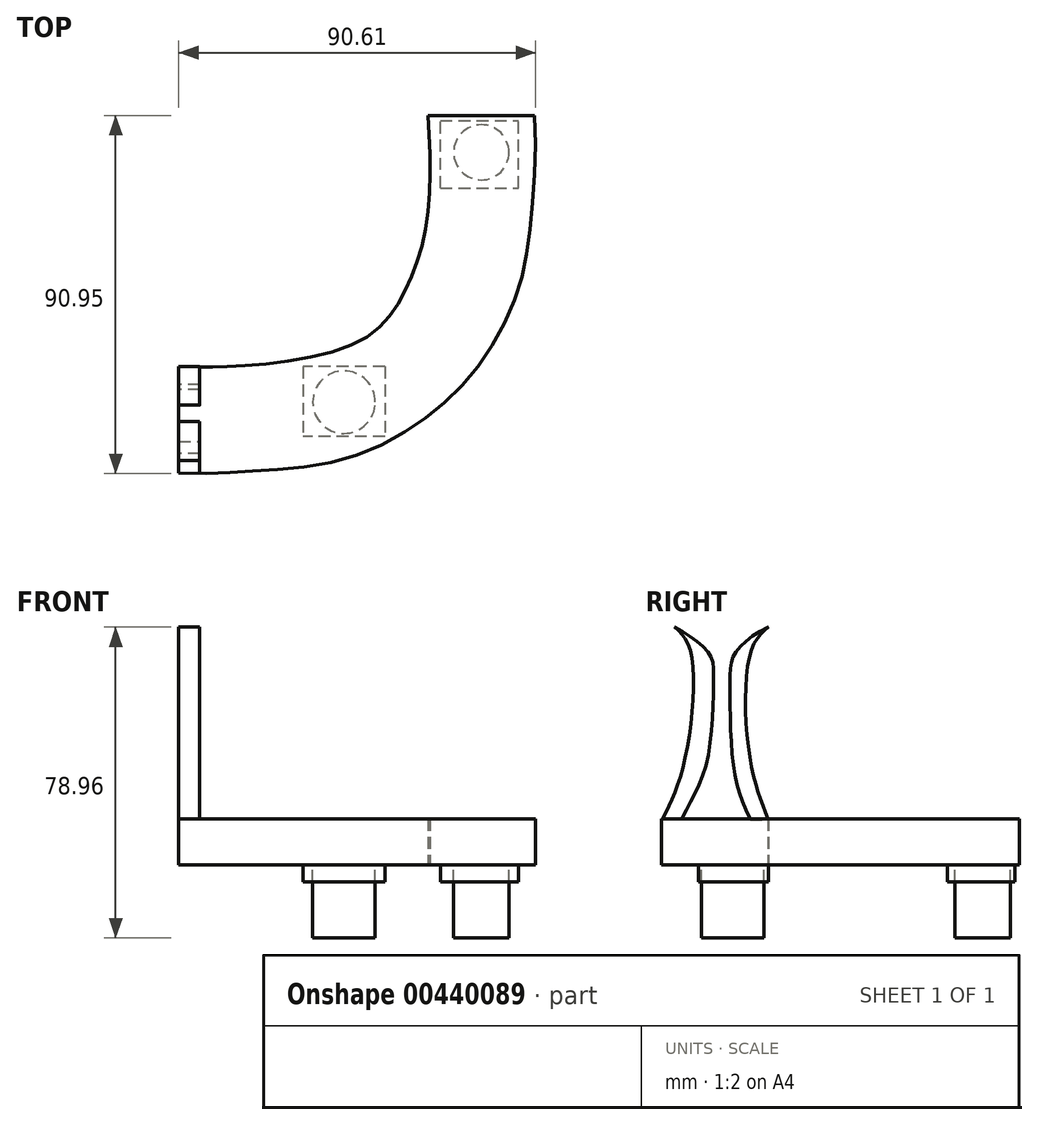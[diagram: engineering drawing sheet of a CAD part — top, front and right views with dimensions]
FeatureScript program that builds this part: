
annotation { "Feature Type Name" : "Feature", "Feature Type Description" : "" }
export const myFeature = defineFeature(function(context is Context, id is Id, definition is map)
    precondition{}
    {
        {
            var Q0;
            Q0=qCreatedBy(makeId("Top.planeOp"),FACE);
            var sketch = newSketch(context, id + "F0", { "sketchPlane" : qUnion([Q0])});
            skLineSegment(sketch, "E0.bottom", {"start": v(-66.47, 45.42) * mm, "end": v(-86.33, 45.42) * mm});
            skLineSegment(sketch, "E0.top", {"start": v(-66.47, 62.56) * mm, "end": v(-86.33, 62.56) * mm});
            skLineSegment(sketch, "E0.left", {"start": v(-66.47, 45.42) * mm, "end": v(-66.47, 62.56) * mm});
            skLineSegment(sketch, "E0.right", {"start": v(-86.33, 45.42) * mm, "end": v(-86.33, 62.56) * mm});
            skLineSegment(sketch, "E1.bottom", {"start": v(-52.34, 0) * mm, "end": v(-31.58, 0) * mm});
            skLineSegment(sketch, "E1.top", {"start": v(-52.34, -17.75) * mm, "end": v(-31.58, -17.75) * mm});
            skLineSegment(sketch, "E1.left", {"start": v(-52.34, 0) * mm, "end": v(-52.34, -17.75) * mm});
            skLineSegment(sketch, "E1.right", {"start": v(-31.58, 0) * mm, "end": v(-31.58, -17.75) * mm});
            skCircle(sketch, "E2", {"center": v(-76.4, 54) * mm, "radius": 7.19 * mm, "construction": true});
            skPoint(sketch, "E2.centerSnap0", {"position": v(-86.33, 54) * mm});
            skLineSegment(sketch, "E3.MirrorCS", {"start": v(66.47, 62.56) * mm, "end": v(86.33, 62.56) * mm});
            skLineSegment(sketch, "E4.MirrorCS", {"start": v(66.47, 45.42) * mm, "end": v(66.47, 62.56) * mm});
            skLineSegment(sketch, "E5.MirrorCS", {"start": v(66.47, 45.42) * mm, "end": v(86.33, 45.42) * mm});
            skLineSegment(sketch, "E6.MirrorCS", {"start": v(86.33, 45.42) * mm, "end": v(86.33, 62.56) * mm});
            skCircle(sketch, "E7.MirrorC", {"center": v(76.4, 54) * mm, "radius": 7.19 * mm, "construction": true});
            skLineSegment(sketch, "E8.MirrorCS", {"start": v(52.34, 0) * mm, "end": v(31.58, 0) * mm});
            skLineSegment(sketch, "E9.MirrorCS", {"start": v(31.58, 0) * mm, "end": v(31.58, -17.75) * mm});
            skLineSegment(sketch, "E10.MirrorCS", {"start": v(52.34, -17.75) * mm, "end": v(31.58, -17.75) * mm});
            skLineSegment(sketch, "E11.MirrorCS", {"start": v(52.34, 0) * mm, "end": v(52.34, -17.75) * mm});
            skSolve(sketch);
        }
        {
            var Q0;
            Q0=qCreatedBy(makeId("Top.planeOp"),FACE);
            var sketch = newSketch(context, id + "F1", { "sketchPlane" : qUnion([Q0])});
            skCircle(sketch, "E12.MirrorC", {"center": v(76.85, 54.44) * mm, "radius": 7.02 * mm});
            skSolve(sketch);
        }
        {
            var Q0;
            Q0=qSketchRegion(id+"F1",true);
            extrude(context, id + "F2", {"entities" : qUnion([Q0]), "oppositeDirection" : true, "depth" : 18.54 * mm});
        }
        {
            var Q0;
            Q0=qCreatedBy(makeId("Top.planeOp"),FACE);
            var sketch = newSketch(context, id + "F3", { "sketchPlane" : qUnion([Q0])});
            skCircle(sketch, "E13.MirrorC", {"center": v(41.96, -9.02) * mm, "radius": 7.95 * mm});
            skSolve(sketch);
        }
        {
            var Q0;
            Q0=qSketchRegion(id+"F3",true);
            extrude(context, id + "F4", {"entities" : qUnion([Q0]), "oppositeDirection" : true, "depth" : 18.54 * mm});
        }
        {
            var Q0;
            Q0=qCreatedBy(makeId("Top.planeOp"),FACE);
            var sketch = newSketch(context, id + "F5", { "sketchPlane" : qUnion([Q0])});
            skLineSegment(sketch, "E14", {"start": v(0, -27.07) * mm, "end": v(0, 0) * mm});
            skFitSpline(sketch, "E15.MirrorCS", {"points": [v(63.32, 63.77) * mm, v(63.02, 36.97) * mm, v(57, 18.35) * mm, v(44.97, 6.02) * mm, v(13.08, 0) * mm, v(0, 0) * mm], "startDerivative": vector(7.76, -117.1) * mm, "endDerivative": vector(-83.43, 0) * mm});
            skFitSpline(sketch, "E16.MirrorCS", {"points": [v(90.42, 63.77) * mm, v(89.44, 36.97) * mm, v(85.82, 18.35) * mm, v(75.95, 0) * mm, v(61.96, -13.5) * mm, v(42.26, -23.46) * mm, v(19.7, -26.47) * mm, v(0, -27.07) * mm], "startDerivative": vector(9.82, -165.02) * mm, "endDerivative": vector(-178.1, 7.05) * mm});
            skLineSegment(sketch, "E17.MirrorCS", {"start": v(90.42, 63.77) * mm, "end": v(63.32, 63.77) * mm});
            skSolve(sketch);
        }
        {
            var Q0;
            Q0=qCreatedBy(makeId("Right.planeOp"),FACE);
            var sketch = newSketch(context, id + "F6", { "sketchPlane" : qUnion([Q0])});
            skFitSpline(sketch, "E18", {"points": [v(-27, 11.42) * mm, v(-21.55, 25.47) * mm, v(-19.64, 53.75) * mm, v(-23.83, 60.42) * mm], "startDerivative": vector(19.37, 38.96) * mm, "endDerivative": vector(-22.3, 19.09) * mm});
            skFitSpline(sketch, "E19", {"points": [v(0, 11.42) * mm, v(-4.4, 25.47) * mm, v(-4.6, 53.75) * mm, v(0, 60.42) * mm], "startDerivative": vector(-14.6, 39.81) * mm, "endDerivative": vector(23.35, 18.46) * mm});
            skFitSpline(sketch, "E20", {"points": [v(-23.83, 60.42) * mm, v(-15.12, 53.75) * mm, v(-13.95, 47.1) * mm, v(-15.82, 25.47) * mm, v(-22.1, 11.42) * mm], "startDerivative": vector(45.4, -24.72) * mm, "endDerivative": vector(-24, -52.8) * mm});
            skFitSpline(sketch, "E21", {"points": [v(0, 60.42) * mm, v(-8.51, 53.75) * mm, v(-9.74, 47.1) * mm, v(-8.9, 25.47) * mm, v(-4.6, 11.42) * mm], "startDerivative": vector(-50.4, -23.74) * mm, "endDerivative": vector(25.2, -53.33) * mm});
            skLineSegment(sketch, "E22", {"start": v(-22.1, 11.42) * mm, "end": v(-27, 11.42) * mm});
            skLineSegment(sketch, "E23", {"start": v(-4.6, 11.42) * mm, "end": v(0, 11.42) * mm});
            skSolve(sketch);
        }
        {
            var Q0;
            Q0=qSketchRegion(id+"F6",true);
            extrude(context, id + "F7", {"entities" : qUnion([Q0]), "depth" : 5.33 * mm});
        }
        {
            var Q0;
            Q0=makeQuery(id+"F5.imprint","IMPRINT",FACE,{"disambiguationData":[TD([[makeQuery(id+"F5.imprint","IMPRINT",EDGE,{"derivedFrom":sQuery(id+"F5.wireOp",EDGE,"E14")}),-1.0]])]});
            extrude(context, id + "F8", {"entities" : qUnion([Q0]), "depth" : 11.68 * mm});
        }
        {
            var Q0;
            Q0=makeQuery(id+"F0.imprint","IMPRINT",FACE,{"disambiguationData":[TD([[makeQuery(id+"F0.imprint","IMPRINT",EDGE,{"derivedFrom":sQuery(id+"F0.wireOp",EDGE,"E8.MirrorCS")}),1.0]])]});
            var Q1;
            Q1=makeQuery(id+"F0.imprint","IMPRINT",FACE,{"disambiguationData":[TD([[makeQuery(id+"F0.imprint","IMPRINT",EDGE,{"derivedFrom":sQuery(id+"F0.wireOp",EDGE,"E3.MirrorCS")}),-1.0]])]});
            extrude(context, id + "F9", {"entities" : qUnion([Q0, Q1]), "oppositeDirection" : true, "depth" : 4.32 * mm});
        }
    });
